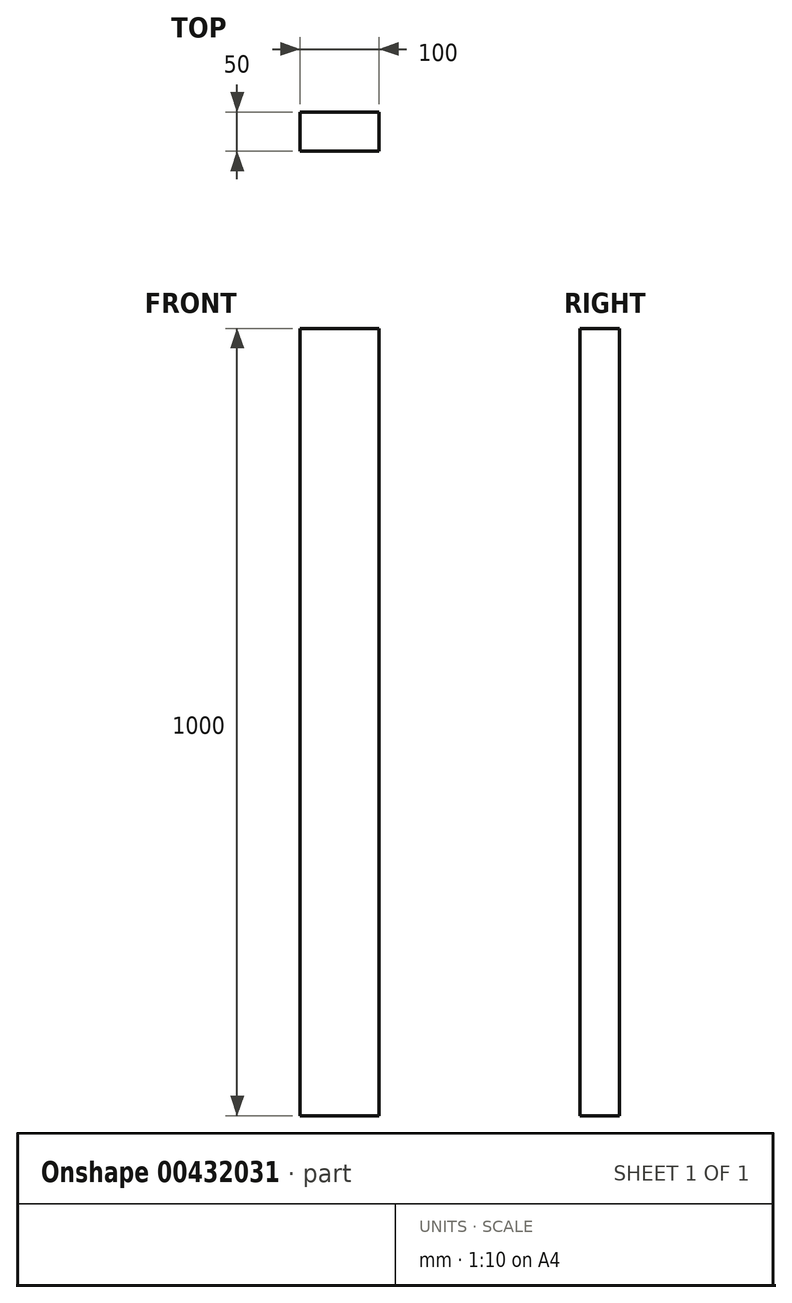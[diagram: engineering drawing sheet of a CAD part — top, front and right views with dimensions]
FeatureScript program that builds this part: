
annotation { "Feature Type Name" : "Feature", "Feature Type Description" : "" }
export const myFeature = defineFeature(function(context is Context, id is Id, definition is map)
    precondition{}
    {
        {
            var Q0;
            Q0=qCreatedBy(makeId("Front.planeOp"),FACE);
            var sketch = newSketch(context, id + "F0", { "sketchPlane" : qUnion([Q0])});
            skLineSegment(sketch, "E0", {"start": v(0, 0) * mm, "end": v(100, 0) * mm});
            skLineSegment(sketch, "E1", {"start": v(100, 0) * mm, "end": v(100, 1000) * mm});
            skLineSegment(sketch, "E2", {"start": v(100, 1000) * mm, "end": v(0, 1000) * mm});
            skLineSegment(sketch, "E3", {"start": v(0, 1000) * mm, "end": v(0, 0) * mm});
            skSolve(sketch);
        }
        {
            var Q0;
            Q0 = qSketchRegion(id + "F0", true);
            extrude(context, id + "F1", {"entities" : qUnion([Q0]), "depth" : 50 * mm});
        }
    });
